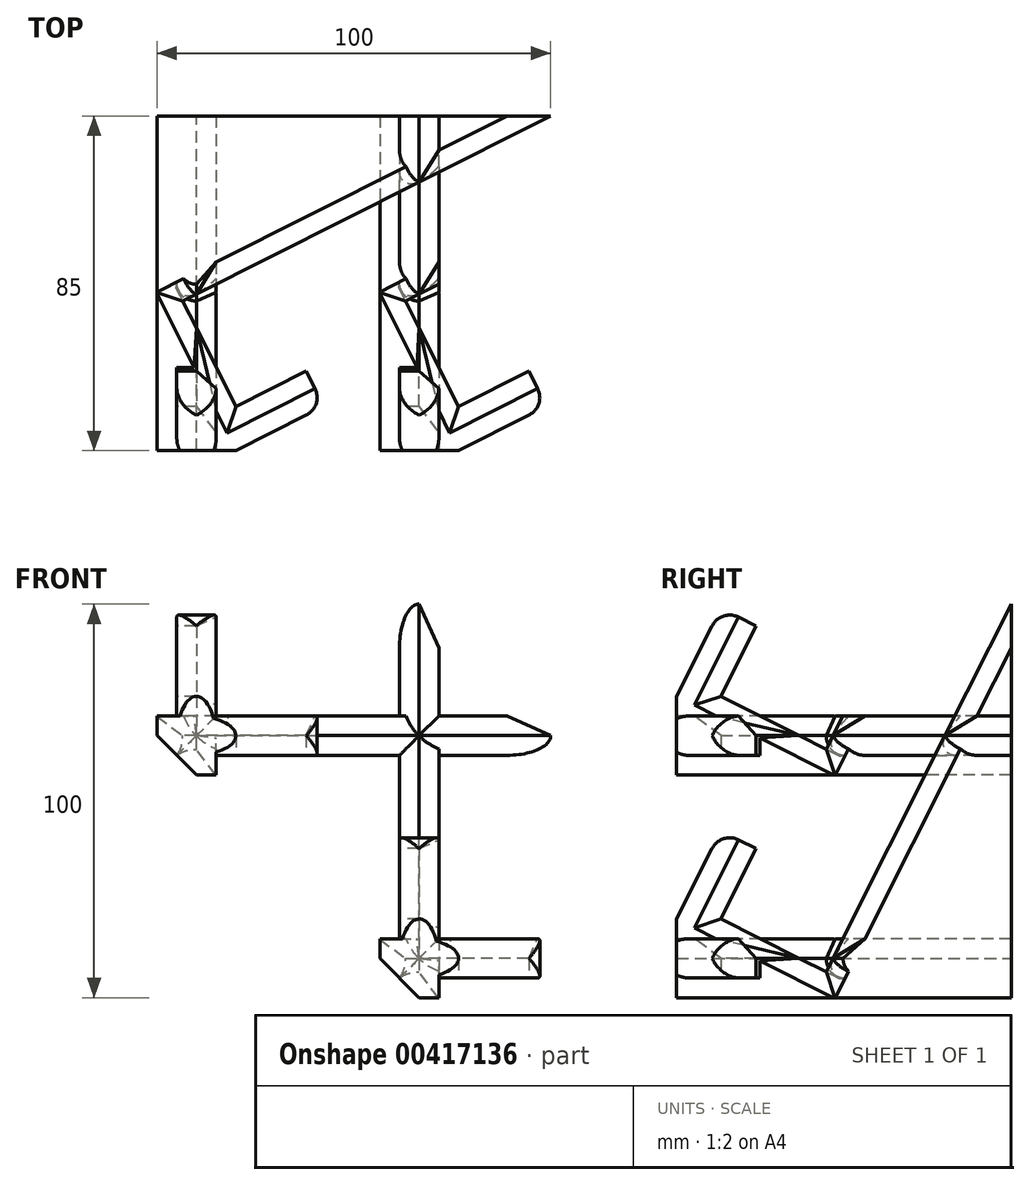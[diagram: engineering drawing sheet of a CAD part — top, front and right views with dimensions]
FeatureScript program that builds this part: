
annotation { "Feature Type Name" : "Feature", "Feature Type Description" : "" }
export const myFeature = defineFeature(function(context is Context, id is Id, definition is map)
    precondition{}
    {
        {
            var Q0;
            Q0=qCreatedBy(makeId("Right.planeOp"),FACE);
            var sketch = newSketch(context, id + "F0", { "sketchPlane" : qUnion([Q0])});
            skLineSegment(sketch, "E0", {"start": v(0, 0) * mm, "end": v(47, 93.48) * mm});
            skLineSegment(sketch, "E1", {"start": v(47, 93.48) * mm, "end": v(47, -6.52) * mm});
            skLineSegment(sketch, "E2", {"start": v(47, -6.52) * mm, "end": v(-38, -6.52) * mm});
            skLineSegment(sketch, "E3", {"start": v(-38, -6.52) * mm, "end": v(-38, 13.48) * mm});
            skLineSegment(sketch, "E4", {"start": v(-38, 13.48) * mm, "end": v(-26.75, 35.84) * mm});
            skLineSegment(sketch, "E5", {"start": v(-26.75, 35.84) * mm, "end": v(-17.82, 31.35) * mm});
            skLineSegment(sketch, "E6", {"start": v(-17.82, 31.35) * mm, "end": v(-26.8, 13.48) * mm});
            skLineSegment(sketch, "E7", {"start": v(-26.8, 13.48) * mm, "end": v(0, 0) * mm});
            skSolve(sketch);
        }
        {
            var Q0;
            Q0 = qSketchRegion(id + "F0", true);
            extrude(context, id + "F1", {"entities" : qUnion([Q0]), "depth" : 10 * mm});
        }
        {
            var Q0;
            Q0=makeQuery(id+"F1.opExtrude","CAP_EDGE",EDGE,{"disambiguationData":[OSD([sQuery(id+"F0.wireOp",EDGE,"E2")])],"isStart":true});
            var Q1;
            Q1=makeQuery(id+"F1.opExtrude","CAP_EDGE",EDGE,{"disambiguationData":[OSD([sQuery(id+"F0.wireOp",EDGE,"E7")])],"isStart":false});
            var Q2;
            Q2=makeQuery(id+"F1.opExtrude","CAP_EDGE",EDGE,{"disambiguationData":[OSD([sQuery(id+"F0.wireOp",EDGE,"E0")])],"isStart":false});
            var Q3;
            Q3=makeQuery(id+"F1.opExtrude","CAP_EDGE",EDGE,{"disambiguationData":[OSD([sQuery(id+"F0.wireOp",EDGE,"E6")])],"isStart":false});
            chamfer(context, id + "F2", {"entities" : qUnion([Q0, Q1, Q2, Q3]), "width" : 5 * mm, "tangentPropagation" : true});
        }
        {
            var Q0;
            Q0=makeQuery(id+"F2.opChamfer","BLEND_FACE",FACE,{"disambiguationData":[OSD([sQuery(id+"F0.wireOp",EDGE,"E2")])]});
            var Q1;
            {var subQ0=sQuery(id+"F0.wireOp",EDGE,"E2");Q1=makeQuery(id+"F2.opChamfer","BLEND_EDGE",EDGE,{"blendedFrom":[makeQuery(id+"F1.opExtrude","CAP_EDGE",EDGE,{"disambiguationData":[OSD([subQ0])],"isStart":true}),makeQuery(id+"F1.opExtrude","CAP_FACE",FACE,{"disambiguationData":[OSD([sQuery(id+"F0.wireOp",EDGE,"E0"),sQuery(id+"F0.wireOp",EDGE,"E1"),subQ0,sQuery(id+"F0.wireOp",EDGE,"E3"),sQuery(id+"F0.wireOp",EDGE,"E4"),sQuery(id+"F0.wireOp",EDGE,"E5"),sQuery(id+"F0.wireOp",EDGE,"E6"),sQuery(id+"F0.wireOp",EDGE,"E7")])],"isStart":true})],"blendedInto":[makeQuery(id+"F1.opExtrude","CAP_FACE",FACE,{"disambiguationData":[OSD([sQuery(id+"F0.wireOp",EDGE,"E0"),sQuery(id+"F0.wireOp",EDGE,"E1"),subQ0,sQuery(id+"F0.wireOp",EDGE,"E3"),sQuery(id+"F0.wireOp",EDGE,"E4"),sQuery(id+"F0.wireOp",EDGE,"E5"),sQuery(id+"F0.wireOp",EDGE,"E6"),sQuery(id+"F0.wireOp",EDGE,"E7")])],"isStart":true})]});}
            cPlane(context, id + "F3", {"entities" : qUnion([Q0, Q1]), "cplaneType" : CPlaneType.LINE_ANGLE, "offset" : 25 * mm, "angle" : 90 * degree, "width" : 150 * mm, "height" : 150 * mm});
        }
        {
            var Q0;
            Q0=qCreatedBy(id+"F3.planeOp",FACE);
            cPlane(context, id + "F4", {"entities" : qUnion([Q0]), "cplaneType" : CPlaneType.OFFSET, "offset" : 40 * mm, "width" : 150 * mm, "height" : 150 * mm});
        }
        {
            var Q0;
            Q0=makeQuery(id+"F9.opPattern","COPY",EDGE,{"derivedFrom":makeQuery(id+"F1.opExtrude","CAP_EDGE",EDGE,{"disambiguationData":[OSD([sQuery(id+"F0.wireOp",EDGE,"E4")])],"isStart":false}),"instanceName":"1"});
            var Q1;
            Q1=makeQuery(id+"F9.opPattern","COPY",EDGE,{"derivedFrom":makeQuery(id+"F1.opExtrude","CAP_EDGE",EDGE,{"disambiguationData":[OSD([sQuery(id+"F0.wireOp",EDGE,"E4")])],"isStart":true}),"instanceName":"1"});
            var Q2;
            Q2=makeQuery(id+"F9.opPattern","COPY",EDGE,{"derivedFrom":makeQuery(id+"F1.opExtrude","SWEPT_EDGE",EDGE,{"disambiguationData":[OSD([sQuery(id+"F0.wireOp",EDGE,"E4"),sQuery(id+"F0.wireOp",EDGE,"E5")])]}),"instanceName":"1"});
            var Q3;
            Q3=makeQuery(id+"F1.opExtrude","CAP_EDGE",EDGE,{"disambiguationData":[OSD([sQuery(id+"F0.wireOp",EDGE,"E4")])],"isStart":true});
            var Q4;
            Q4=makeQuery(id+"F1.opExtrude","CAP_EDGE",EDGE,{"disambiguationData":[OSD([sQuery(id+"F0.wireOp",EDGE,"E4")])],"isStart":false});
            var Q5;
            Q5=makeQuery(id+"F1.opExtrude","SWEPT_EDGE",EDGE,{"disambiguationData":[OSD([sQuery(id+"F0.wireOp",EDGE,"E4"),sQuery(id+"F0.wireOp",EDGE,"E5")])]});
            var Q6;
            {var subQ0=sQuery(id+"F0.wireOp",EDGE,"E0");var subQ1=makeQuery(id+"F1.opExtrude","SWEPT_FACE",FACE,{"disambiguationData":[OSD([subQ0])]});Q6=makeQuery(id+"F9.boolean.opBoolean","SPLIT",EDGE,{"disambiguationData":[TD([subQ1])],"derivedFrom":makeQuery(id+"F9.opPattern","COPY",EDGE,{"derivedFrom":makeQuery(id+"F1.opExtrude","CAP_EDGE",EDGE,{"disambiguationData":[OSD([subQ0])],"isStart":true}),"instanceName":"1"})});}
            var Q7;
            {var subQ0=sQuery(id+"F0.wireOp",EDGE,"E0");var subQ2=sQuery(id+"F0.wireOp",EDGE,"E7");Q7=makeQuery(id+"F9.boolean.opBoolean","SPLIT",EDGE,{"disambiguationData":[TD([makeQuery(id+"F1.opExtrude","SWEPT_FACE",FACE,{"disambiguationData":[OSD([subQ2])]})])],"derivedFrom":makeQuery(id+"F1.opExtrude","CAP_EDGE",EDGE,{"disambiguationData":[OSD([subQ0])],"isStart":true})});}
            var Q8;
            {var subQ0=sQuery(id+"F0.wireOp",EDGE,"E1");var subQ1=sQuery(id+"F0.wireOp",EDGE,"E0");var subQ2=makeQuery(id+"F1.opExtrude","SWEPT_FACE",FACE,{"disambiguationData":[OSD([subQ0])]});Q8=makeQuery(id+"F9.boolean.opBoolean","SPLIT",EDGE,{"disambiguationData":[TD([subQ2])],"derivedFrom":makeQuery(id+"F9.opPattern","COPY",EDGE,{"derivedFrom":makeQuery(id+"F1.opExtrude","CAP_EDGE",EDGE,{"disambiguationData":[OSD([subQ1])],"isStart":true}),"instanceName":"1"})});}
            var Q9;
            {var subQ0=sQuery(id+"F0.wireOp",EDGE,"E1");var subQ1=makeQuery(id+"F1.opExtrude","SWEPT_FACE",FACE,{"disambiguationData":[OSD([subQ0])]});var subQ2=sQuery(id+"F0.wireOp",EDGE,"E0");Q9=makeQuery(id+"F9.boolean.opBoolean","SPLIT",EDGE,{"disambiguationData":[TD([subQ1])],"derivedFrom":makeQuery(id+"F1.opExtrude","CAP_EDGE",EDGE,{"disambiguationData":[OSD([subQ2])],"isStart":true})});}
            fillet(context, id + "F5", {"entities" : qUnion([Q0, Q1, Q2, Q3, Q4, Q5, Q6, Q7, Q8, Q9]), "radius" : 5 * mm, "tangentPropagation" : true, "allowEdgeOverflow" : false});
        }
        {
            var Q0;
            Q0=makeQuery(id+"F1.opExtrude","SWEPT_BODY",BODY,{"disambiguationData":[OSD([sQuery(id+"F0.wireOp",EDGE,"E0"),sQuery(id+"F0.wireOp",EDGE,"E1"),sQuery(id+"F0.wireOp",EDGE,"E2"),sQuery(id+"F0.wireOp",EDGE,"E3"),sQuery(id+"F0.wireOp",EDGE,"E4"),sQuery(id+"F0.wireOp",EDGE,"E5"),sQuery(id+"F0.wireOp",EDGE,"E6"),sQuery(id+"F0.wireOp",EDGE,"E7")])]});
            var Q1;
            Q1=qCreatedBy(id+"F3.planeOp",FACE);
            mirror(context, id + "F6", {"operationType" : NewBodyOperationType.ADD, "entities" : qUnion([Q0]), "mirrorPlane" : qUnion([Q1])});
        }
        {
            var Q0;
            {var subQ0=sQuery(id+"F0.wireOp",EDGE,"E1");var subQ1=sQuery(id+"F0.wireOp",EDGE,"E0");var subQ2=makeQuery(id+"F2.opChamfer","SPLIT",FACE,{"disambiguationData":[OD(1.0)],"derivedFrom":makeQuery(id+"F1.opExtrude","CAP_FACE",FACE,{"disambiguationData":[OSD([subQ1,subQ0,sQuery(id+"F0.wireOp",EDGE,"E2"),sQuery(id+"F0.wireOp",EDGE,"E3"),sQuery(id+"F0.wireOp",EDGE,"E4"),sQuery(id+"F0.wireOp",EDGE,"E5"),sQuery(id+"F0.wireOp",EDGE,"E6"),sQuery(id+"F0.wireOp",EDGE,"E7")])],"isStart":false})});var subQ4=makeQuery(id+"F2.opChamfer","BLEND_FACE",FACE,{"disambiguationData":[OSD([subQ1])]});Q0=makeQuery(id+"F6.boolean.opBoolean","SPLIT",FACE,{"disambiguationData":[TD([makeQuery(id+"F6.opPattern","COPY",FACE,{"derivedFrom":subQ4,"instanceName":"1"})])],"derivedFrom":subQ2});}
            var sketch = newSketch(context, id + "F7", { "sketchPlane" : qUnion([Q0])});
            skLineSegment(sketch, "E8.bottom", {"start": v(1.48, 100.33) * mm, "end": v(118, 100.33) * mm});
            skLineSegment(sketch, "E8.top", {"start": v(1.48, -61.85) * mm, "end": v(118, -61.85) * mm});
            skLineSegment(sketch, "E8.left", {"start": v(1.48, 100.33) * mm, "end": v(1.48, -61.85) * mm});
            skLineSegment(sketch, "E8.right", {"start": v(118, 100.33) * mm, "end": v(118, -61.85) * mm});
            skSolve(sketch);
        }
        {
            var Q0;
            Q0 = qSketchRegion(id + "F7", true);
            extrude(context, id + "F8", {"entities" : qUnion([Q0]), "operationType" : NewBodyOperationType.REMOVE, "endBound" : BoundingType.THROUGH_ALL, "depth" : 25 * mm});
        }
        {
            var Q0;
            Q0=makeQuery(id+"F1.opExtrude","SWEPT_BODY",BODY,{"disambiguationData":[OSD([sQuery(id+"F0.wireOp",EDGE,"E0"),sQuery(id+"F0.wireOp",EDGE,"E1"),sQuery(id+"F0.wireOp",EDGE,"E2"),sQuery(id+"F0.wireOp",EDGE,"E3"),sQuery(id+"F0.wireOp",EDGE,"E4"),sQuery(id+"F0.wireOp",EDGE,"E5"),sQuery(id+"F0.wireOp",EDGE,"E6"),sQuery(id+"F0.wireOp",EDGE,"E7")])]});
            var Q1;
            Q1=qCreatedBy(id+"F4.planeOp",FACE);
            mirror(context, id + "F9", {"operationType" : NewBodyOperationType.ADD, "entities" : qUnion([Q0]), "mirrorPlane" : qUnion([Q1])});
        }
    });
